# Revit family: Accessory-Towel_Warmer-KOHLER-STILLNESS-K-45132T_1
name_source: partatom
category: Plumbing Fixtures
revit_build: Autodesk Revit 2017 (Build: 20160225_1515(x64)
units: mm (PartAtom-declared; Revit-internal decimal feet)

## family parameters
Cut with Voids When Loaded = No
Host = Face
OmniClass Number = 23.31.25.25.13
OmniClass Title = Water Heated Towel Bars
Part Type = Normal
Room Calculation Point = No
Round Connector Dimension = Use Diameter
Shared = No

## types (1)
- CP-Polished Chrome
    ADA Compliant = No
    Assembly Code = C1030200
    CW Connection = No
    Date Modified = 06/11/2021
    Default Elevation = 42"
    Description = TOWEL WARMER , WATER SUPPLY
    Finish = Kohler-Metal-CP-Polished_Chrome
    HW Connection = Yes
    Height = 20 5/8"
    Length = 9 1/8"
    Manufacturer = KOHLER Co.
    Master Format 2014 = 10 28 00
    Master Format 2014 Name = Toilet, Bath, and Laundry Accessories
    Material = Premium Metal Construction
    Model = K-45132T-CP
    Product Name = STILLNESS
    Tempared Water Inlet = Tempared Water Inlet
    Tempared Water Outlet = Tempared Water Outlet
    Type = 1
    URL = http://www.kohler.com.cn
    Vent Connection = No
    Waste Connection = No
    WaterSense Certified = No
    Width = 24"

## geometry (parser evidence)
native form markers: Sweep x5
no freeform markers — native parametric forms only
